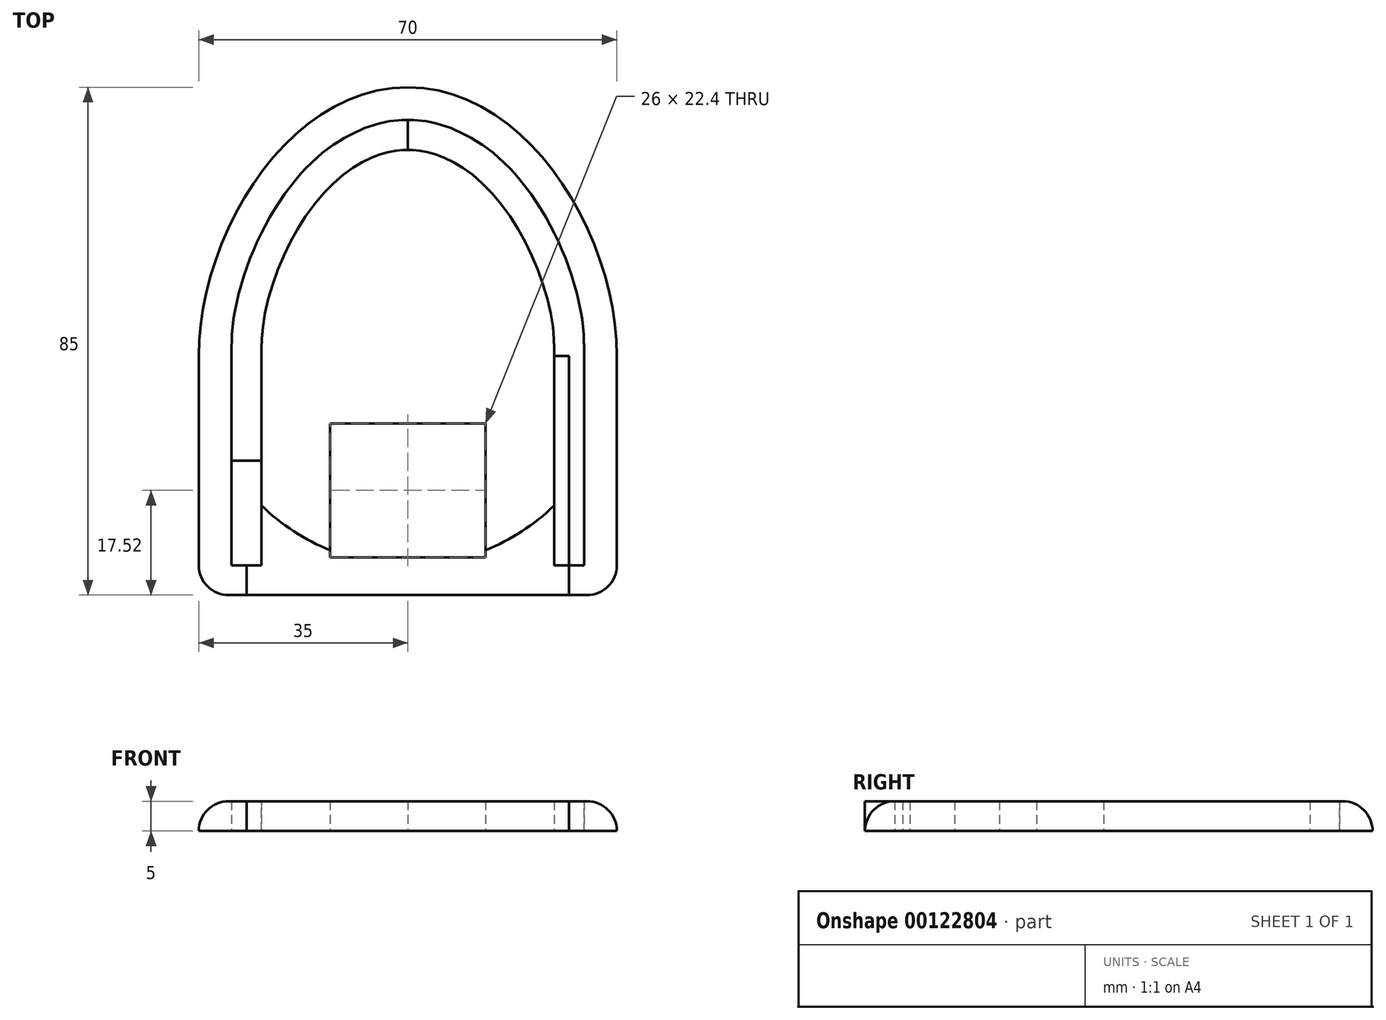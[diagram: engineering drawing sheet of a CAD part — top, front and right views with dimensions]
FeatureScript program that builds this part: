
annotation { "Feature Type Name" : "Feature", "Feature Type Description" : "" }
export const myFeature = defineFeature(function(context is Context, id is Id, definition is map)
    precondition{}
    {
        {
            var Q0;
            Q0=qCreatedBy(makeId("Top.planeOp"),FACE);
            var sketch = newSketch(context, id + "F0", { "sketchPlane" : qUnion([Q0])});
            skLineSegment(sketch, "E0.top", {"start": v(-35, -40) * mm, "end": v(35, -40) * mm});
            skPoint(sketch, "E0.middle", {"position": v(0, 13.14) * mm});
            skPoint(sketch, "E1", {"position": v(0, 0) * mm});
            skCircle(sketch, "E2", {"center": v(0, 0) * mm, "radius": 35 * mm});
            skPoint(sketch, "E3.visualSharp", {"position": v(-35, -40) * mm});
            skPoint(sketch, "E4.visualSharp", {"position": v(35, -40) * mm});
            skPoint(sketch, "E5", {"position": v(-35, 0) * mm});
            skPoint(sketch, "E6", {"position": v(35, 0) * mm});
            skFitSpline(sketch, "E7", {"points": [v(0, 45) * mm, v(-35, 0) * mm], "startDerivative": vector(-60.6, 0) * mm, "endDerivative": vector(0, -60.15) * mm});
            skLineSegment(sketch, "E8", {"start": v(-35, 0) * mm, "end": v(-35, -40) * mm});
            skLineSegment(sketch, "E9", {"start": v(35, 0) * mm, "end": v(35, -40) * mm});
            skFitSpline(sketch, "E10.MirrorCS", {"points": [v(0, 45) * mm, v(35, 0) * mm], "startDerivative": vector(60.6, 0) * mm, "endDerivative": vector(0, -60.15) * mm});
            skFitSpline(sketch, "E11.0", {"points": [v(0, 37) * mm, v(-0.85, 37) * mm, v(-2.51, 36.87) * mm, v(-4.95, 36.3) * mm, v(-7.36, 35.37) * mm, v(-10.54, 33.64) * mm, v(-14.42, 30.55) * mm, v(-18.67, 25.54) * mm, v(-22.24, 19.56) * mm, v(-24.95, 13) * mm, v(-26.62, 6.3) * mm, v(-27, 2.01) * mm, v(-27, 0) * mm]});
            skLineSegment(sketch, "E12", {"start": v(-27, 0) * mm, "end": v(-27, -40) * mm});
            skPoint(sketch, "E13", {"position": v(-27, -35) * mm});
            skLineSegment(sketch, "E14.MirrorCS", {"start": v(27, 0) * mm, "end": v(27, -40) * mm});
            skPoint(sketch, "E15.MirrorP", {"position": v(27, -35) * mm});
            skFitSpline(sketch, "E16.0", {"points": [v(0, 37) * mm, v(0.85, 37) * mm, v(2.51, 36.87) * mm, v(4.95, 36.3) * mm, v(7.36, 35.37) * mm, v(10.54, 33.64) * mm, v(14.42, 30.55) * mm, v(18.67, 25.54) * mm, v(22.24, 19.56) * mm, v(24.95, 13) * mm, v(26.62, 6.3) * mm, v(27, 2.01) * mm, v(27, 0) * mm]});
            skLineSegment(sketch, "E17.bottom", {"start": v(-29.5, 0) * mm, "end": v(-24.5, 0) * mm});
            skLineSegment(sketch, "E17.top", {"start": v(-29.5, -35) * mm, "end": v(-24.5, -35) * mm});
            skLineSegment(sketch, "E17.left", {"start": v(-29.5, 0) * mm, "end": v(-29.5, -35) * mm});
            skLineSegment(sketch, "E17.right", {"start": v(-24.5, 0) * mm, "end": v(-24.5, -35) * mm});
            skFitSpline(sketch, "E18.0", {"points": [v(0, 39.5) * mm, v(-0.98, 39.5) * mm, v(-2.9, 39.35) * mm, v(-5.7, 38.7) * mm, v(-8.42, 37.65) * mm, v(-11.97, 35.7) * mm, v(-16.2, 32.33) * mm, v(-20.72, 26.99) * mm, v(-24.49, 20.68) * mm, v(-27.33, 13.8) * mm, v(-29.1, 6.72) * mm, v(-29.5, 2.17) * mm, v(-29.5, 0) * mm]});
            skFitSpline(sketch, "E19.1", {"points": [v(0, 34.5) * mm, v(-0.72, 34.5) * mm, v(-2.13, 34.39) * mm, v(-4.2, 33.91) * mm, v(-6.3, 33.1) * mm, v(-9.11, 31.57) * mm, v(-12.65, 28.76) * mm, v(-16.62, 24.1) * mm, v(-20, 18.44) * mm, v(-22.56, 12.22) * mm, v(-24.15, 5.87) * mm, v(-24.5, 1.86) * mm, v(-24.5, 0) * mm]});
            skFitSpline(sketch, "E19.2", {"points": [v(0, 34.5) * mm, v(0.72, 34.5) * mm, v(2.13, 34.39) * mm, v(4.2, 33.91) * mm, v(6.3, 33.1) * mm, v(9.11, 31.57) * mm, v(12.65, 28.76) * mm, v(16.62, 24.1) * mm, v(20, 18.44) * mm, v(22.56, 12.22) * mm, v(24.15, 5.87) * mm, v(24.5, 1.86) * mm, v(24.5, 0) * mm]});
            skLineSegment(sketch, "E19.3", {"start": v(24.5, 0) * mm, "end": v(24.5, -35) * mm});
            skFitSpline(sketch, "E20.0", {"points": [v(0, 39.5) * mm, v(0.98, 39.5) * mm, v(2.9, 39.35) * mm, v(5.7, 38.7) * mm, v(8.42, 37.65) * mm, v(11.97, 35.7) * mm, v(16.2, 32.33) * mm, v(20.72, 26.99) * mm, v(24.49, 20.68) * mm, v(27.33, 13.8) * mm, v(29.1, 6.72) * mm, v(29.5, 2.17) * mm, v(29.5, 0) * mm]});
            skLineSegment(sketch, "E21.bottom", {"start": v(29.5, 0) * mm, "end": v(24.5, 0) * mm});
            skLineSegment(sketch, "E21.top", {"start": v(29.5, -35) * mm, "end": v(24.5, -35) * mm});
            skLineSegment(sketch, "E21.left", {"start": v(29.5, 0) * mm, "end": v(29.5, -35) * mm});
            skLineSegment(sketch, "E22", {"start": v(-29.5, -17.5) * mm, "end": v(-24.5, -17.5) * mm});
            skLineSegment(sketch, "E23", {"start": v(0, 39.5) * mm, "end": v(0, 34.5) * mm});
            skLineSegment(sketch, "E24.bottom", {"start": v(-13, -11.28) * mm, "end": v(13, -11.28) * mm});
            skLineSegment(sketch, "E24.top", {"start": v(-13, -33.68) * mm, "end": v(13, -33.68) * mm});
            skLineSegment(sketch, "E24.left", {"start": v(-13, -11.28) * mm, "end": v(-13, -33.68) * mm});
            skLineSegment(sketch, "E24.right", {"start": v(13, -11.28) * mm, "end": v(13, -33.68) * mm});
            skPoint(sketch, "E24.middle", {"position": v(0, -22.48) * mm});
            skLineSegment(sketch, "E25", {"start": v(-18.92, -7.73) * mm, "end": v(19.66, -7.73) * mm});
            skSolve(sketch);
        }
        {
            var Q0;
            Q0=qSketchRegion(id+"F0",true);
            var Q1;
            {var subQ4=sQuery(id+"F0.wireOp",EDGE,"E19.1");Q1=makeQuery(id+"F0.imprint","IMPRINT",FACE,{"disambiguationData":[TD([[makeQuery(id+"F0.imprint","IMPRINT",EDGE,{"derivedFrom":subQ4}),1.0]])]});}
            var Q2;
            {var subQ0=sQuery(id+"F0.wireOp",EDGE,"E24.top");var subQ1=sQuery(id+"F0.wireOp",EDGE,"E2");var subQ2=makeQuery(id+"F0.imprint","INTERSECT",VERTEX,{"disambiguationData":[OD(0.0)],"derivedFrom":[subQ1,subQ0]});Q2=makeQuery(id+"F0.imprint","IMPRINT",FACE,{"disambiguationData":[TD([[makeQuery(id+"F0.imprint","IMPRINT",EDGE,{"disambiguationData":[TD([[subQ2,-1.0]])],"derivedFrom":subQ1}),1.0]])]});}
            extrude(context, id + "F1", {"entities" : qUnion([Q0, Q1, Q2]), "depth" : 5 * mm});
        }
        {
            var Q0;
            Q0=makeQuery(id+"F1.opExtrude","SWEPT_EDGE",EDGE,{"disambiguationData":[OSD([sQuery(id+"F0.wireOp",EDGE,"E0.top"),sQuery(id+"F0.wireOp",EDGE,"E8")])]});
            var Q1;
            Q1=makeQuery(id+"F1.opExtrude","SWEPT_EDGE",EDGE,{"disambiguationData":[OSD([sQuery(id+"F0.wireOp",EDGE,"E0.top"),sQuery(id+"F0.wireOp",EDGE,"E9")])]});
            var Q2;
            Q2=makeQuery(id+"F1.opExtrude","CAP_EDGE",EDGE,{"disambiguationData":[OSD([sQuery(id+"F0.wireOp",EDGE,"E8")])],"isStart":false});
            var Q3;
            Q3=makeQuery(id+"F1.opExtrude","CAP_EDGE",EDGE,{"disambiguationData":[OSD([sQuery(id+"F0.wireOp",EDGE,"E0.top")])],"isStart":false});
            fillet(context, id + "F2", {"entities" : qUnion([Q0, Q1, Q2, Q3]), "radius" : 5 * mm, "tangentPropagation" : true, "allowEdgeOverflow" : false});
        }
        {
            var Q0;
            {var subQ0=sQuery(id+"F0.wireOp",EDGE,"E19.3");var subQ1=sQuery(id+"F0.wireOp",EDGE,"E2");var subQ2=makeQuery(id+"F0.imprint","INTERSECT",VERTEX,{"derivedFrom":[subQ1,subQ0]});Q0=makeQuery(id+"F0.imprint","IMPRINT",FACE,{"disambiguationData":[TD([[makeQuery(id+"F0.imprint","IMPRINT",EDGE,{"disambiguationData":[TD([[subQ2,-1.0]])],"derivedFrom":subQ1}),-1.0]])]});}
            var Q1;
            {var subQ0=sQuery(id+"F0.wireOp",EDGE,"E14.MirrorCS");var subQ1=sQuery(id+"F0.wireOp",EDGE,"E2");var subQ2=makeQuery(id+"F0.imprint","INTERSECT",VERTEX,{"derivedFrom":[subQ1,subQ0]});Q1=makeQuery(id+"F0.imprint","IMPRINT",FACE,{"disambiguationData":[TD([[makeQuery(id+"F0.imprint","IMPRINT",EDGE,{"disambiguationData":[TD([[subQ2,-1.0]])],"derivedFrom":subQ1}),-1.0]])]});}
            var Q2;
            {var subQ0=sQuery(id+"F0.wireOp",EDGE,"E19.3");var subQ1=sQuery(id+"F0.wireOp",EDGE,"E2");var subQ2=makeQuery(id+"F0.imprint","INTERSECT",VERTEX,{"derivedFrom":[subQ1,subQ0]});Q2=makeQuery(id+"F0.imprint","IMPRINT",FACE,{"disambiguationData":[TD([[makeQuery(id+"F0.imprint","IMPRINT",EDGE,{"disambiguationData":[TD([[subQ2,-1.0]])],"derivedFrom":subQ1}),1.0]])]});}
            var Q3;
            {var subQ0=sQuery(id+"F0.wireOp",EDGE,"E14.MirrorCS");var subQ1=sQuery(id+"F0.wireOp",EDGE,"E2");var subQ2=makeQuery(id+"F0.imprint","INTERSECT",VERTEX,{"derivedFrom":[subQ1,subQ0]});Q3=makeQuery(id+"F0.imprint","IMPRINT",FACE,{"disambiguationData":[TD([[makeQuery(id+"F0.imprint","IMPRINT",EDGE,{"disambiguationData":[TD([[subQ2,-1.0]])],"derivedFrom":subQ1}),1.0]])]});}
            var Q4;
            {var subQ3=sQuery(id+"F0.wireOp",EDGE,"E19.2");Q4=makeQuery(id+"F0.imprint","IMPRINT",FACE,{"disambiguationData":[TD([[makeQuery(id+"F0.imprint","IMPRINT",EDGE,{"derivedFrom":subQ3}),1.0]])]});}
            var Q5;
            {var subQ0=sQuery(id+"F0.wireOp",EDGE,"E20.0");var subQ1=sQuery(id+"F0.wireOp",EDGE,"E2");var subQ2=makeQuery(id+"F0.imprint","INTERSECT",VERTEX,{"derivedFrom":[subQ1,subQ0]});Q5=makeQuery(id+"F0.imprint","IMPRINT",FACE,{"disambiguationData":[TD([[makeQuery(id+"F0.imprint","IMPRINT",EDGE,{"disambiguationData":[TD([[subQ2,-1.0]])],"derivedFrom":subQ1}),1.0]])]});}
            var Q6;
            {var subQ0=sQuery(id+"F0.wireOp",EDGE,"E16.0");var subQ1=sQuery(id+"F0.wireOp",EDGE,"E2");var subQ2=makeQuery(id+"F0.imprint","INTERSECT",VERTEX,{"derivedFrom":[subQ1,subQ0]});Q6=makeQuery(id+"F0.imprint","IMPRINT",FACE,{"disambiguationData":[TD([[makeQuery(id+"F0.imprint","IMPRINT",EDGE,{"disambiguationData":[TD([[subQ2,-1.0]])],"derivedFrom":subQ1}),-1.0]])]});}
            var Q7;
            {var subQ0=sQuery(id+"F0.wireOp",EDGE,"E20.0");var subQ1=sQuery(id+"F0.wireOp",EDGE,"E2");var subQ2=makeQuery(id+"F0.imprint","INTERSECT",VERTEX,{"derivedFrom":[subQ1,subQ0]});Q7=makeQuery(id+"F0.imprint","IMPRINT",FACE,{"disambiguationData":[TD([[makeQuery(id+"F0.imprint","IMPRINT",EDGE,{"disambiguationData":[TD([[subQ2,-1.0]])],"derivedFrom":subQ1}),-1.0]])]});}
            var Q8;
            {var subQ0=sQuery(id+"F0.wireOp",EDGE,"E12");var subQ1=sQuery(id+"F0.wireOp",EDGE,"E2");var subQ2=makeQuery(id+"F0.imprint","INTERSECT",VERTEX,{"derivedFrom":[subQ1,subQ0]});Q8=makeQuery(id+"F0.imprint","IMPRINT",FACE,{"disambiguationData":[TD([[makeQuery(id+"F0.imprint","IMPRINT",EDGE,{"disambiguationData":[TD([[subQ2,-1.0]])],"derivedFrom":subQ1}),1.0]])]});}
            var Q9;
            {var subQ0=sQuery(id+"F0.wireOp",EDGE,"E17.left");var subQ1=sQuery(id+"F0.wireOp",EDGE,"E2");var subQ2=makeQuery(id+"F0.imprint","INTERSECT",VERTEX,{"derivedFrom":[subQ1,subQ0]});Q9=makeQuery(id+"F0.imprint","IMPRINT",FACE,{"disambiguationData":[TD([[makeQuery(id+"F0.imprint","IMPRINT",EDGE,{"disambiguationData":[TD([[subQ2,-1.0]])],"derivedFrom":subQ1}),1.0]])]});}
            var Q10;
            {var subQ0=sQuery(id+"F0.wireOp",EDGE,"E17.left");var subQ1=sQuery(id+"F0.wireOp",EDGE,"E2");var subQ2=makeQuery(id+"F0.imprint","INTERSECT",VERTEX,{"derivedFrom":[subQ1,subQ0]});Q10=makeQuery(id+"F0.imprint","IMPRINT",FACE,{"disambiguationData":[TD([[makeQuery(id+"F0.imprint","IMPRINT",EDGE,{"disambiguationData":[TD([[subQ2,-1.0]])],"derivedFrom":subQ1}),-1.0]])]});}
            var Q11;
            {var subQ0=sQuery(id+"F0.wireOp",EDGE,"E12");var subQ1=sQuery(id+"F0.wireOp",EDGE,"E2");var subQ2=makeQuery(id+"F0.imprint","INTERSECT",VERTEX,{"derivedFrom":[subQ1,subQ0]});Q11=makeQuery(id+"F0.imprint","IMPRINT",FACE,{"disambiguationData":[TD([[makeQuery(id+"F0.imprint","IMPRINT",EDGE,{"disambiguationData":[TD([[subQ2,-1.0]])],"derivedFrom":subQ1}),-1.0]])]});}
            extrude(context, id + "F3", {"entities" : qUnion([Q0, Q1, Q2, Q3, Q4, Q5, Q6, Q7, Q8, Q9, Q10, Q11]), "depth" : 5 * mm});
        }
        {
            var Q0;
            {var subQ3=sQuery(id+"F0.wireOp",EDGE,"E22");var subQ5=sQuery(id+"F0.wireOp",EDGE,"E17.left");var subQ7=makeQuery(id+"F0.imprint","INTERSECT",VERTEX,{"derivedFrom":[subQ5,subQ3]});Q0=makeQuery(id+"F0.imprint","IMPRINT",FACE,{"disambiguationData":[TD([[makeQuery(id+"F0.imprint","IMPRINT",EDGE,{"disambiguationData":[TD([[subQ7,-1.0]])],"derivedFrom":subQ3}),1.0]])]});}
            var Q1;
            {var subQ3=sQuery(id+"F0.wireOp",EDGE,"E22");var subQ5=sQuery(id+"F0.wireOp",EDGE,"E17.right");var subQ7=makeQuery(id+"F0.imprint","INTERSECT",VERTEX,{"derivedFrom":[subQ5,subQ3]});Q1=makeQuery(id+"F0.imprint","IMPRINT",FACE,{"disambiguationData":[TD([[makeQuery(id+"F0.imprint","IMPRINT",EDGE,{"disambiguationData":[TD([[subQ7,1.0]])],"derivedFrom":subQ3}),1.0]])]});}
            var Q2;
            {var subQ0=sQuery(id+"F0.wireOp",EDGE,"E11.0");var subQ1=sQuery(id+"F0.wireOp",EDGE,"E2");var subQ2=makeQuery(id+"F0.imprint","INTERSECT",VERTEX,{"derivedFrom":[subQ1,subQ0]});Q2=makeQuery(id+"F0.imprint","IMPRINT",FACE,{"disambiguationData":[TD([[makeQuery(id+"F0.imprint","IMPRINT",EDGE,{"disambiguationData":[TD([[subQ2,-1.0]])],"derivedFrom":subQ1}),1.0]])]});}
            var Q3;
            {var subQ0=sQuery(id+"F0.wireOp",EDGE,"E19.1");Q3=makeQuery(id+"F0.imprint","IMPRINT",FACE,{"disambiguationData":[TD([[makeQuery(id+"F0.imprint","IMPRINT",EDGE,{"derivedFrom":subQ0}),-1.0]])]});}
            var Q4;
            {var subQ0=sQuery(id+"F0.wireOp",EDGE,"E23");var subQ1=sQuery(id+"F0.wireOp",EDGE,"E2");var subQ2=makeQuery(id+"F0.imprint","INTERSECT",VERTEX,{"derivedFrom":[subQ1,subQ0]});Q4=makeQuery(id+"F0.imprint","IMPRINT",FACE,{"disambiguationData":[TD([[makeQuery(id+"F0.imprint","IMPRINT",EDGE,{"disambiguationData":[TD([[subQ2,-1.0]])],"derivedFrom":subQ1}),-1.0]])]});}
            var Q5;
            {var subQ0=sQuery(id+"F0.wireOp",EDGE,"E11.0");var subQ1=sQuery(id+"F0.wireOp",EDGE,"E2");var subQ2=makeQuery(id+"F0.imprint","INTERSECT",VERTEX,{"derivedFrom":[subQ1,subQ0]});Q5=makeQuery(id+"F0.imprint","IMPRINT",FACE,{"disambiguationData":[TD([[makeQuery(id+"F0.imprint","IMPRINT",EDGE,{"disambiguationData":[TD([[subQ2,-1.0]])],"derivedFrom":subQ1}),-1.0]])]});}
            extrude(context, id + "F4", {"entities" : qUnion([Q0, Q1, Q2, Q3, Q4, Q5]), "depth" : 5 * mm});
        }
    });
